# Revit family: Bernhardt_Design-Seating-Guest-Chantal_wood
name_source: partatom
category: Furniture
revit_build: Autodesk Revit 2016 (Build: 20150714_1515(x64)
units: mm (PartAtom-declared; Revit-internal decimal feet)

## family parameters
Always vertical = Yes
Cut with Voids When Loaded = No
OmniClass Number = 23.40.20.00
OmniClass Title = General Furniture and Specialties
Room Calculation Point = No
Shared = No
Work Plane-Based = No

## types (5) — shared parameters
Manufacturer = Bernhardt Design
Model = Chantal
URL = http://www.bernhardtdesign.com

## per-type parameters (varying)
| type | Base | Cast Base | Tubular Base | Type Selection | Wood Base | Wood Base Material |
| Chantal 1023 | Chrome | No | Yes | 1023 | No |  |
| Chantal 1023K | Matte Black Powdercoat Aluminum | No | Yes | 10231 | No |  |
| Chantal 1024K | Matte Black Powdercoat Aluminum | Yes | No | 10241 | No |  |
| Chantal 1024 | Polished Aluminum | Yes | No | 1024 | No |  |
| Chantal 1026M |  | No | No | 1026 | Yes | <By Category> |

## geometry (parser evidence)
native form markers: Sweep x5
no freeform markers — native parametric forms only
